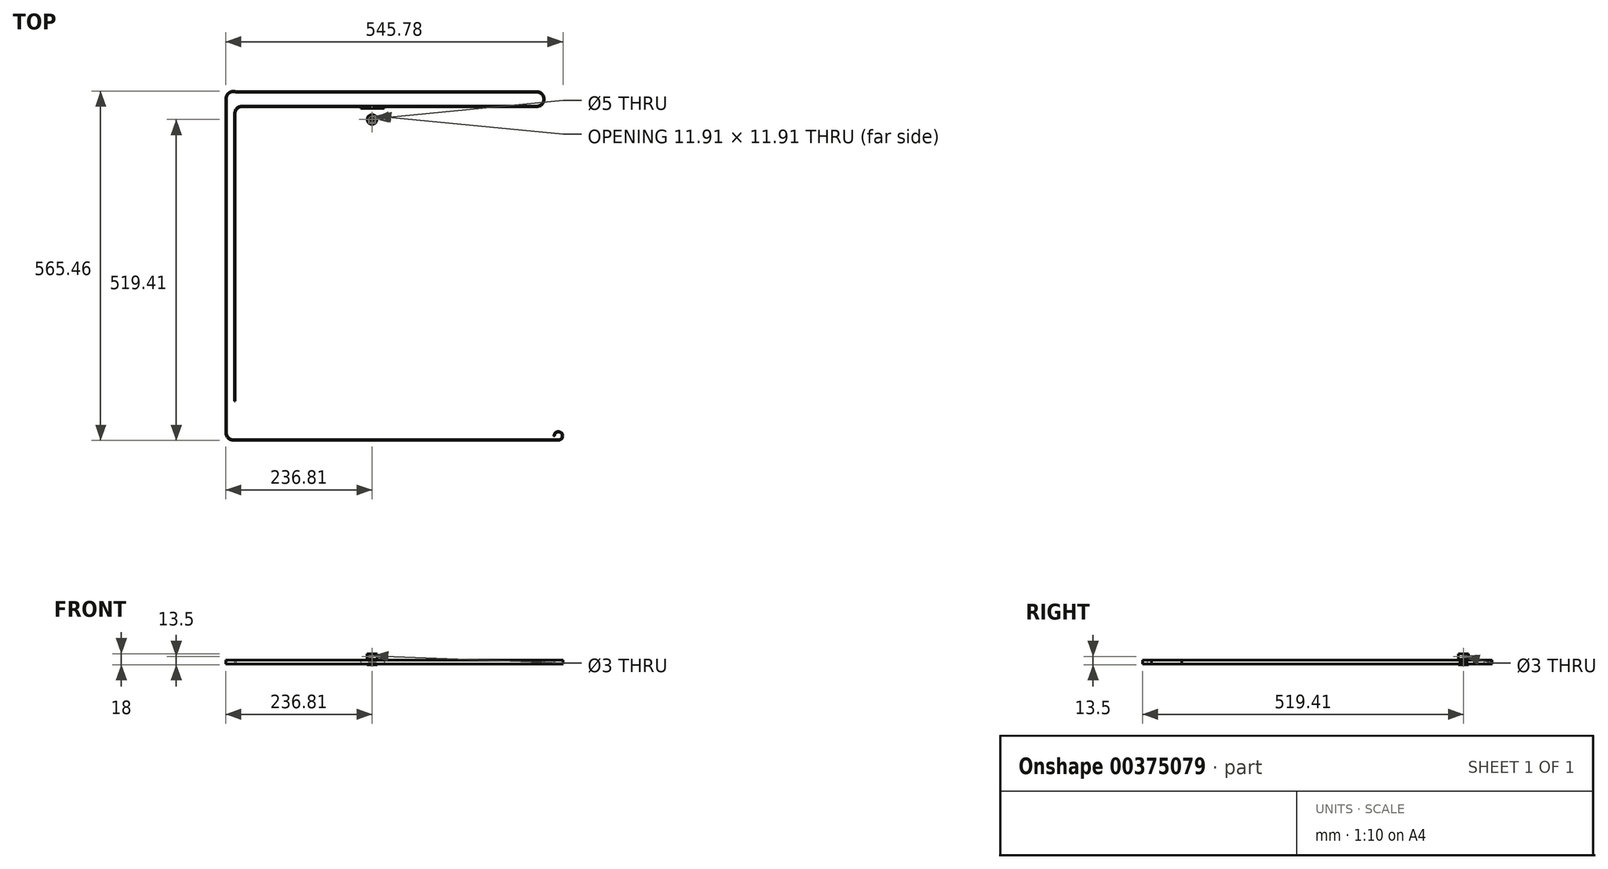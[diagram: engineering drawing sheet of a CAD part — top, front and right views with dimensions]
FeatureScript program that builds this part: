
annotation { "Feature Type Name" : "Feature", "Feature Type Description" : "" }
export const myFeature = defineFeature(function(context is Context, id is Id, definition is map)
    precondition{}
    {
        {
            var Q0;
            Q0=qCreatedBy(makeId("Top.planeOp"),FACE);
            var sketch = newSketch(context, id + "F0", { "sketchPlane" : qUnion([Q0])});
            skLineSegment(sketch, "E0", {"start": v(-19.17, 17.78) * mm, "end": v(-18.17, 17.78) * mm});
            skLineSegment(sketch, "E1", {"start": v(-18.17, 17.78) * mm, "end": v(-18.17, 18.4) * mm});
            skArc(sketch, "E2", {"start": v(-18.67, 18.85) * mm, "mid": v(-18.88, 19.07) * mm, "end": v(-19.17, 19.16) * mm});
            skArc(sketch, "E3", {"start": v(-18.58, 18.54) * mm, "mid": v(-18.61, 18.7) * mm, "end": v(-18.67, 18.85) * mm});
            skArc(sketch, "E4", {"start": v(-18.58, 18.54) * mm, "mid": v(-18.53, 18.44) * mm, "end": v(-18.43, 18.4) * mm});
            skLineSegment(sketch, "E5", {"start": v(-18.43, 18.4) * mm, "end": v(-18.17, 18.4) * mm});
            skArc(sketch, "E6.0.MirrorCS", {"start": v(-19.67, 18.85) * mm, "mid": v(-19.47, 19.07) * mm, "end": v(-19.17, 19.16) * mm});
            skArc(sketch, "E7.0.MirrorCS", {"start": v(-19.76, 18.54) * mm, "mid": v(-19.73, 18.7) * mm, "end": v(-19.67, 18.85) * mm});
            skArc(sketch, "E8.0.MirrorCS", {"start": v(-19.76, 18.54) * mm, "mid": v(-19.81, 18.44) * mm, "end": v(-19.91, 18.4) * mm});
            skLineSegment(sketch, "E9.0.MirrorCS", {"start": v(-19.91, 18.4) * mm, "end": v(-20.17, 18.4) * mm});
            skLineSegment(sketch, "E10.0.MirrorCS", {"start": v(-20.17, 17.78) * mm, "end": v(-20.17, 18.4) * mm});
            skLineSegment(sketch, "E11.0.MirrorCS", {"start": v(-19.17, 17.78) * mm, "end": v(-20.17, 17.78) * mm});
            skLineSegment(sketch, "E12.direction1", {"start": v(-20.17, 17.78) * mm, "end": v(-18.17, 17.78) * mm, "construction": true});
            skLineSegment(sketch, "E13", {"start": v(-20.17, 18.15) * mm, "end": v(-18.17, 18.15) * mm, "construction": true});
            skPoint(sketch, "E14", {"position": v(0, -5.25) * mm});
            skArc(sketch, "E15", {"start": v(0.51, -5.6) * mm, "mid": v(0, -5.25) * mm, "end": v(-0.51, -5.6) * mm});
            skArc(sketch, "E16", {"start": v(-0.51, -5.6) * mm, "mid": v(-0.56, -5.71) * mm, "end": v(-0.59, -5.83) * mm});
            skArc(sketch, "E17", {"start": v(0.59, -5.83) * mm, "mid": v(0.56, -5.71) * mm, "end": v(0.51, -5.6) * mm});
            skArc(sketch, "E18", {"start": v(0.72, -5.96) * mm, "mid": v(0.94, -5.93) * mm, "end": v(1.16, -5.89) * mm});
            skArc(sketch, "E19", {"start": v(0.59, -5.83) * mm, "mid": v(0.66, -5.94) * mm, "end": v(0.8, -5.95) * mm});
            skArc(sketch, "E20", {"start": v(-0.59, -5.83) * mm, "mid": v(-0.66, -5.94) * mm, "end": v(-0.8, -5.95) * mm});
            skArc(sketch, "E21.1.0", {"start": v(2.22, -5.16) * mm, "mid": v(1.62, -5) * mm, "end": v(1.24, -5.48) * mm});
            skPoint(sketch, "E21.1.1", {"position": v(1.62, -5) * mm});
            skArc(sketch, "E21.1.2", {"start": v(1.24, -5.48) * mm, "mid": v(1.23, -5.6) * mm, "end": v(1.24, -5.73) * mm});
            skArc(sketch, "E21.1.3", {"start": v(2.36, -5.37) * mm, "mid": v(2.47, -5.44) * mm, "end": v(2.6, -5.41) * mm});
            skArc(sketch, "E21.1.4", {"start": v(1.24, -5.73) * mm, "mid": v(1.2, -5.85) * mm, "end": v(1.08, -5.9) * mm});
            skArc(sketch, "E21.1.5", {"start": v(2.36, -5.37) * mm, "mid": v(2.3, -5.26) * mm, "end": v(2.22, -5.16) * mm});
            skArc(sketch, "E22.3.2.0", {"start": v(3.7, -4.22) * mm, "mid": v(3.09, -4.25) * mm, "end": v(2.87, -4.83) * mm});
            skPoint(sketch, "E22.4.2.0", {"position": v(3.09, -4.25) * mm});
            skArc(sketch, "E22.5.2.0", {"start": v(2.87, -4.83) * mm, "mid": v(2.9, -4.95) * mm, "end": v(2.95, -5.07) * mm});
            skArc(sketch, "E22.9.2.0", {"start": v(3.9, -4.37) * mm, "mid": v(4.03, -4.41) * mm, "end": v(4.14, -4.35) * mm});
            skArc(sketch, "E22.13.2.0", {"start": v(2.95, -5.07) * mm, "mid": v(2.95, -5.2) * mm, "end": v(2.85, -5.28) * mm});
            skArc(sketch, "E22.17.2.0", {"start": v(3.9, -4.37) * mm, "mid": v(3.81, -4.3) * mm, "end": v(3.7, -4.22) * mm});
            skArc(sketch, "E22.3.3.0", {"start": v(4.83, -2.87) * mm, "mid": v(4.25, -3.09) * mm, "end": v(4.22, -3.7) * mm});
            skPoint(sketch, "E22.4.3.0", {"position": v(4.25, -3.09) * mm});
            skArc(sketch, "E22.5.3.0", {"start": v(4.22, -3.7) * mm, "mid": v(4.3, -3.81) * mm, "end": v(4.37, -3.9) * mm});
            skArc(sketch, "E22.9.3.0", {"start": v(5.07, -2.95) * mm, "mid": v(5.2, -2.95) * mm, "end": v(5.28, -2.85) * mm});
            skArc(sketch, "E22.13.3.0", {"start": v(4.37, -3.9) * mm, "mid": v(4.41, -4.03) * mm, "end": v(4.35, -4.14) * mm});
            skArc(sketch, "E22.17.3.0", {"start": v(5.07, -2.95) * mm, "mid": v(4.95, -2.9) * mm, "end": v(4.83, -2.87) * mm});
            skArc(sketch, "E22.3.4.0", {"start": v(5.48, -1.24) * mm, "mid": v(5, -1.62) * mm, "end": v(5.16, -2.22) * mm});
            skPoint(sketch, "E22.4.4.0", {"position": v(5, -1.62) * mm});
            skArc(sketch, "E22.5.4.0", {"start": v(5.16, -2.22) * mm, "mid": v(5.26, -2.3) * mm, "end": v(5.37, -2.36) * mm});
            skArc(sketch, "E22.9.4.0", {"start": v(5.73, -1.24) * mm, "mid": v(5.85, -1.2) * mm, "end": v(5.9, -1.08) * mm});
            skArc(sketch, "E22.13.4.0", {"start": v(5.37, -2.36) * mm, "mid": v(5.44, -2.47) * mm, "end": v(5.41, -2.6) * mm});
            skArc(sketch, "E22.17.4.0", {"start": v(5.73, -1.24) * mm, "mid": v(5.6, -1.23) * mm, "end": v(5.48, -1.24) * mm});
            skArc(sketch, "E22.3.5.0", {"start": v(5.6, 0.51) * mm, "mid": v(5.25, 0) * mm, "end": v(5.6, -0.51) * mm});
            skPoint(sketch, "E22.4.5.0", {"position": v(5.25, 0) * mm});
            skArc(sketch, "E22.5.5.0", {"start": v(5.6, -0.51) * mm, "mid": v(5.71, -0.56) * mm, "end": v(5.83, -0.59) * mm});
            skArc(sketch, "E22.9.5.0", {"start": v(5.83, 0.59) * mm, "mid": v(5.94, 0.66) * mm, "end": v(5.95, 0.8) * mm});
            skArc(sketch, "E22.13.5.0", {"start": v(5.83, -0.59) * mm, "mid": v(5.94, -0.66) * mm, "end": v(5.95, -0.8) * mm});
            skArc(sketch, "E22.17.5.0", {"start": v(5.83, 0.59) * mm, "mid": v(5.71, 0.56) * mm, "end": v(5.6, 0.51) * mm});
            skArc(sketch, "E22.3.6.0", {"start": v(5.16, 2.22) * mm, "mid": v(5, 1.62) * mm, "end": v(5.48, 1.24) * mm});
            skPoint(sketch, "E22.4.6.0", {"position": v(5, 1.62) * mm});
            skArc(sketch, "E22.5.6.0", {"start": v(5.48, 1.24) * mm, "mid": v(5.6, 1.23) * mm, "end": v(5.73, 1.24) * mm});
            skArc(sketch, "E22.9.6.0", {"start": v(5.37, 2.36) * mm, "mid": v(5.44, 2.47) * mm, "end": v(5.41, 2.6) * mm});
            skArc(sketch, "E22.13.6.0", {"start": v(5.73, 1.24) * mm, "mid": v(5.85, 1.2) * mm, "end": v(5.9, 1.08) * mm});
            skArc(sketch, "E22.17.6.0", {"start": v(5.37, 2.36) * mm, "mid": v(5.26, 2.3) * mm, "end": v(5.16, 2.22) * mm});
            skArc(sketch, "E22.3.7.0", {"start": v(4.22, 3.7) * mm, "mid": v(4.25, 3.09) * mm, "end": v(4.83, 2.87) * mm});
            skPoint(sketch, "E22.4.7.0", {"position": v(4.25, 3.09) * mm});
            skArc(sketch, "E22.5.7.0", {"start": v(4.83, 2.87) * mm, "mid": v(4.95, 2.9) * mm, "end": v(5.07, 2.95) * mm});
            skArc(sketch, "E22.9.7.0", {"start": v(4.37, 3.9) * mm, "mid": v(4.41, 4.03) * mm, "end": v(4.35, 4.14) * mm});
            skArc(sketch, "E22.13.7.0", {"start": v(5.07, 2.95) * mm, "mid": v(5.2, 2.95) * mm, "end": v(5.28, 2.85) * mm});
            skArc(sketch, "E22.17.7.0", {"start": v(4.37, 3.9) * mm, "mid": v(4.3, 3.81) * mm, "end": v(4.22, 3.7) * mm});
            skArc(sketch, "E22.3.8.0", {"start": v(2.87, 4.83) * mm, "mid": v(3.09, 4.25) * mm, "end": v(3.7, 4.22) * mm});
            skPoint(sketch, "E22.4.8.0", {"position": v(3.09, 4.25) * mm});
            skArc(sketch, "E22.5.8.0", {"start": v(3.7, 4.22) * mm, "mid": v(3.81, 4.3) * mm, "end": v(3.9, 4.37) * mm});
            skArc(sketch, "E22.9.8.0", {"start": v(2.95, 5.07) * mm, "mid": v(2.95, 5.2) * mm, "end": v(2.85, 5.28) * mm});
            skArc(sketch, "E22.13.8.0", {"start": v(3.9, 4.37) * mm, "mid": v(4.03, 4.41) * mm, "end": v(4.14, 4.35) * mm});
            skArc(sketch, "E22.17.8.0", {"start": v(2.95, 5.07) * mm, "mid": v(2.9, 4.95) * mm, "end": v(2.87, 4.83) * mm});
            skArc(sketch, "E22.3.9.0", {"start": v(1.24, 5.48) * mm, "mid": v(1.62, 5) * mm, "end": v(2.22, 5.16) * mm});
            skPoint(sketch, "E22.4.9.0", {"position": v(1.62, 5) * mm});
            skArc(sketch, "E22.5.9.0", {"start": v(2.22, 5.16) * mm, "mid": v(2.3, 5.26) * mm, "end": v(2.36, 5.37) * mm});
            skArc(sketch, "E22.9.9.0", {"start": v(1.24, 5.73) * mm, "mid": v(1.2, 5.85) * mm, "end": v(1.08, 5.9) * mm});
            skArc(sketch, "E22.13.9.0", {"start": v(2.36, 5.37) * mm, "mid": v(2.47, 5.44) * mm, "end": v(2.6, 5.41) * mm});
            skArc(sketch, "E22.17.9.0", {"start": v(1.24, 5.73) * mm, "mid": v(1.23, 5.6) * mm, "end": v(1.24, 5.48) * mm});
            skArc(sketch, "E22.3.10.0", {"start": v(-0.51, 5.6) * mm, "mid": v(0, 5.25) * mm, "end": v(0.51, 5.6) * mm});
            skPoint(sketch, "E22.4.10.0", {"position": v(0, 5.25) * mm});
            skArc(sketch, "E22.5.10.0", {"start": v(0.51, 5.6) * mm, "mid": v(0.56, 5.71) * mm, "end": v(0.59, 5.83) * mm});
            skArc(sketch, "E22.9.10.0", {"start": v(-0.59, 5.83) * mm, "mid": v(-0.66, 5.94) * mm, "end": v(-0.8, 5.95) * mm});
            skArc(sketch, "E22.13.10.0", {"start": v(0.59, 5.83) * mm, "mid": v(0.66, 5.94) * mm, "end": v(0.8, 5.95) * mm});
            skArc(sketch, "E22.17.10.0", {"start": v(-0.59, 5.83) * mm, "mid": v(-0.56, 5.71) * mm, "end": v(-0.51, 5.6) * mm});
            skArc(sketch, "E22.3.11.0", {"start": v(-2.22, 5.16) * mm, "mid": v(-1.62, 5) * mm, "end": v(-1.24, 5.48) * mm});
            skPoint(sketch, "E22.4.11.0", {"position": v(-1.62, 5) * mm});
            skArc(sketch, "E22.5.11.0", {"start": v(-1.24, 5.48) * mm, "mid": v(-1.23, 5.6) * mm, "end": v(-1.24, 5.73) * mm});
            skArc(sketch, "E22.9.11.0", {"start": v(-2.36, 5.37) * mm, "mid": v(-2.47, 5.44) * mm, "end": v(-2.6, 5.41) * mm});
            skArc(sketch, "E22.13.11.0", {"start": v(-1.24, 5.73) * mm, "mid": v(-1.2, 5.85) * mm, "end": v(-1.08, 5.9) * mm});
            skArc(sketch, "E22.17.11.0", {"start": v(-2.36, 5.37) * mm, "mid": v(-2.3, 5.26) * mm, "end": v(-2.22, 5.16) * mm});
            skArc(sketch, "E22.3.12.0", {"start": v(-3.7, 4.22) * mm, "mid": v(-3.09, 4.25) * mm, "end": v(-2.87, 4.83) * mm});
            skPoint(sketch, "E22.4.12.0", {"position": v(-3.09, 4.25) * mm});
            skArc(sketch, "E22.5.12.0", {"start": v(-2.87, 4.83) * mm, "mid": v(-2.9, 4.95) * mm, "end": v(-2.95, 5.07) * mm});
            skArc(sketch, "E22.9.12.0", {"start": v(-3.9, 4.37) * mm, "mid": v(-4.03, 4.41) * mm, "end": v(-4.14, 4.35) * mm});
            skArc(sketch, "E22.13.12.0", {"start": v(-2.95, 5.07) * mm, "mid": v(-2.95, 5.2) * mm, "end": v(-2.85, 5.28) * mm});
            skArc(sketch, "E22.17.12.0", {"start": v(-3.9, 4.37) * mm, "mid": v(-3.81, 4.3) * mm, "end": v(-3.7, 4.22) * mm});
            skArc(sketch, "E22.3.13.0", {"start": v(-4.83, 2.87) * mm, "mid": v(-4.25, 3.09) * mm, "end": v(-4.22, 3.7) * mm});
            skPoint(sketch, "E22.4.13.0", {"position": v(-4.25, 3.09) * mm});
            skArc(sketch, "E22.5.13.0", {"start": v(-4.22, 3.7) * mm, "mid": v(-4.3, 3.81) * mm, "end": v(-4.37, 3.9) * mm});
            skArc(sketch, "E22.9.13.0", {"start": v(-5.07, 2.95) * mm, "mid": v(-5.2, 2.95) * mm, "end": v(-5.28, 2.85) * mm});
            skArc(sketch, "E22.13.13.0", {"start": v(-4.37, 3.9) * mm, "mid": v(-4.41, 4.03) * mm, "end": v(-4.35, 4.14) * mm});
            skArc(sketch, "E22.17.13.0", {"start": v(-5.07, 2.95) * mm, "mid": v(-4.95, 2.9) * mm, "end": v(-4.83, 2.87) * mm});
            skArc(sketch, "E22.3.14.0", {"start": v(-5.48, 1.24) * mm, "mid": v(-5, 1.62) * mm, "end": v(-5.16, 2.22) * mm});
            skPoint(sketch, "E22.4.14.0", {"position": v(-5, 1.62) * mm});
            skArc(sketch, "E22.5.14.0", {"start": v(-5.16, 2.22) * mm, "mid": v(-5.26, 2.3) * mm, "end": v(-5.37, 2.36) * mm});
            skArc(sketch, "E22.9.14.0", {"start": v(-5.73, 1.24) * mm, "mid": v(-5.85, 1.2) * mm, "end": v(-5.9, 1.08) * mm});
            skArc(sketch, "E22.13.14.0", {"start": v(-5.37, 2.36) * mm, "mid": v(-5.44, 2.47) * mm, "end": v(-5.41, 2.6) * mm});
            skArc(sketch, "E22.17.14.0", {"start": v(-5.73, 1.24) * mm, "mid": v(-5.6, 1.23) * mm, "end": v(-5.48, 1.24) * mm});
            skArc(sketch, "E22.3.15.0", {"start": v(-5.6, -0.51) * mm, "mid": v(-5.25, 0) * mm, "end": v(-5.6, 0.51) * mm});
            skPoint(sketch, "E22.4.15.0", {"position": v(-5.25, 0) * mm});
            skArc(sketch, "E22.5.15.0", {"start": v(-5.6, 0.51) * mm, "mid": v(-5.71, 0.56) * mm, "end": v(-5.83, 0.59) * mm});
            skArc(sketch, "E22.9.15.0", {"start": v(-5.83, -0.59) * mm, "mid": v(-5.94, -0.66) * mm, "end": v(-5.95, -0.8) * mm});
            skArc(sketch, "E22.13.15.0", {"start": v(-5.83, 0.59) * mm, "mid": v(-5.94, 0.66) * mm, "end": v(-5.95, 0.8) * mm});
            skArc(sketch, "E22.17.15.0", {"start": v(-5.83, -0.59) * mm, "mid": v(-5.71, -0.56) * mm, "end": v(-5.6, -0.51) * mm});
            skArc(sketch, "E22.3.16.0", {"start": v(-5.16, -2.22) * mm, "mid": v(-5, -1.62) * mm, "end": v(-5.48, -1.24) * mm});
            skPoint(sketch, "E22.4.16.0", {"position": v(-5, -1.62) * mm});
            skArc(sketch, "E22.5.16.0", {"start": v(-5.48, -1.24) * mm, "mid": v(-5.6, -1.23) * mm, "end": v(-5.73, -1.24) * mm});
            skArc(sketch, "E22.9.16.0", {"start": v(-5.37, -2.36) * mm, "mid": v(-5.44, -2.47) * mm, "end": v(-5.41, -2.6) * mm});
            skArc(sketch, "E22.13.16.0", {"start": v(-5.73, -1.24) * mm, "mid": v(-5.85, -1.2) * mm, "end": v(-5.9, -1.08) * mm});
            skArc(sketch, "E22.17.16.0", {"start": v(-5.37, -2.36) * mm, "mid": v(-5.26, -2.3) * mm, "end": v(-5.16, -2.22) * mm});
            skArc(sketch, "E22.3.17.0", {"start": v(-4.22, -3.7) * mm, "mid": v(-4.25, -3.09) * mm, "end": v(-4.83, -2.87) * mm});
            skPoint(sketch, "E22.4.17.0", {"position": v(-4.25, -3.09) * mm});
            skArc(sketch, "E22.5.17.0", {"start": v(-4.83, -2.87) * mm, "mid": v(-4.95, -2.9) * mm, "end": v(-5.07, -2.95) * mm});
            skArc(sketch, "E22.9.17.0", {"start": v(-4.37, -3.9) * mm, "mid": v(-4.41, -4.03) * mm, "end": v(-4.35, -4.14) * mm});
            skArc(sketch, "E22.13.17.0", {"start": v(-5.07, -2.95) * mm, "mid": v(-5.2, -2.95) * mm, "end": v(-5.28, -2.85) * mm});
            skArc(sketch, "E22.17.17.0", {"start": v(-4.37, -3.9) * mm, "mid": v(-4.3, -3.81) * mm, "end": v(-4.22, -3.7) * mm});
            skArc(sketch, "E22.3.18.0", {"start": v(-2.87, -4.83) * mm, "mid": v(-3.09, -4.25) * mm, "end": v(-3.7, -4.22) * mm});
            skPoint(sketch, "E22.4.18.0", {"position": v(-3.09, -4.25) * mm});
            skArc(sketch, "E22.5.18.0", {"start": v(-3.7, -4.22) * mm, "mid": v(-3.81, -4.3) * mm, "end": v(-3.9, -4.37) * mm});
            skArc(sketch, "E22.9.18.0", {"start": v(-2.95, -5.07) * mm, "mid": v(-2.95, -5.2) * mm, "end": v(-2.85, -5.28) * mm});
            skArc(sketch, "E22.13.18.0", {"start": v(-3.9, -4.37) * mm, "mid": v(-4.03, -4.41) * mm, "end": v(-4.14, -4.35) * mm});
            skArc(sketch, "E22.17.18.0", {"start": v(-2.95, -5.07) * mm, "mid": v(-2.9, -4.95) * mm, "end": v(-2.87, -4.83) * mm});
            skArc(sketch, "E22.3.19.0", {"start": v(-1.24, -5.48) * mm, "mid": v(-1.62, -5) * mm, "end": v(-2.22, -5.16) * mm});
            skPoint(sketch, "E22.4.19.0", {"position": v(-1.62, -5) * mm});
            skArc(sketch, "E22.5.19.0", {"start": v(-2.22, -5.16) * mm, "mid": v(-2.3, -5.26) * mm, "end": v(-2.36, -5.37) * mm});
            skArc(sketch, "E22.9.19.0", {"start": v(-1.24, -5.73) * mm, "mid": v(-1.2, -5.85) * mm, "end": v(-1.08, -5.9) * mm});
            skArc(sketch, "E22.13.19.0", {"start": v(-2.36, -5.37) * mm, "mid": v(-2.47, -5.44) * mm, "end": v(-2.6, -5.41) * mm});
            skArc(sketch, "E22.17.19.0", {"start": v(-1.24, -5.73) * mm, "mid": v(-1.23, -5.6) * mm, "end": v(-1.24, -5.48) * mm});
            skArc(sketch, "E23.trimOffspring", {"start": v(2.52, -5.44) * mm, "mid": v(2.72, -5.35) * mm, "end": v(2.92, -5.24) * mm});
            skArc(sketch, "E24.trimOffspring", {"start": v(4.08, -4.4) * mm, "mid": v(4.24, -4.24) * mm, "end": v(4.4, -4.08) * mm});
            skArc(sketch, "E25.trimOffspring", {"start": v(5.24, -2.92) * mm, "mid": v(5.33, -2.76) * mm, "end": v(5.41, -2.6) * mm});
            skArc(sketch, "E26.trimOffspring", {"start": v(5.89, -1.16) * mm, "mid": v(5.93, -0.94) * mm, "end": v(5.96, -0.72) * mm});
            skArc(sketch, "E27.trimOffspring", {"start": v(5.44, 2.52) * mm, "mid": v(5.35, 2.72) * mm, "end": v(5.24, 2.92) * mm});
            skArc(sketch, "E28.trimOffspring", {"start": v(4.4, 4.08) * mm, "mid": v(4.24, 4.24) * mm, "end": v(4.08, 4.4) * mm});
            skArc(sketch, "E29.trimOffspring", {"start": v(5.96, 0.72) * mm, "mid": v(5.93, 0.94) * mm, "end": v(5.89, 1.16) * mm});
            skArc(sketch, "E30.trimOffspring", {"start": v(2.92, 5.24) * mm, "mid": v(2.72, 5.35) * mm, "end": v(2.52, 5.44) * mm});
            skArc(sketch, "E31.trimOffspring", {"start": v(1.16, 5.89) * mm, "mid": v(0.94, 5.93) * mm, "end": v(0.72, 5.96) * mm});
            skArc(sketch, "E32.trimOffspring", {"start": v(-0.72, 5.96) * mm, "mid": v(-0.94, 5.93) * mm, "end": v(-1.16, 5.89) * mm});
            skArc(sketch, "E33.trimOffspring", {"start": v(-2.52, 5.44) * mm, "mid": v(-2.72, 5.35) * mm, "end": v(-2.92, 5.24) * mm});
            skArc(sketch, "E34.trimOffspring", {"start": v(-4.08, 4.4) * mm, "mid": v(-4.24, 4.24) * mm, "end": v(-4.4, 4.08) * mm});
            skArc(sketch, "E35.trimOffspring", {"start": v(-5.24, 2.92) * mm, "mid": v(-5.35, 2.72) * mm, "end": v(-5.44, 2.52) * mm});
            skArc(sketch, "E36.trimOffspring", {"start": v(-5.89, 1.16) * mm, "mid": v(-5.93, 0.94) * mm, "end": v(-5.96, 0.72) * mm});
            skArc(sketch, "E37.trimOffspring", {"start": v(-5.96, -0.72) * mm, "mid": v(-5.93, -0.94) * mm, "end": v(-5.89, -1.16) * mm});
            skArc(sketch, "E38.trimOffspring", {"start": v(-5.44, -2.52) * mm, "mid": v(-5.35, -2.72) * mm, "end": v(-5.24, -2.92) * mm});
            skArc(sketch, "E39.trimOffspring", {"start": v(-4.4, -4.08) * mm, "mid": v(-4.24, -4.24) * mm, "end": v(-4.08, -4.4) * mm});
            skArc(sketch, "E40.trimOffspring", {"start": v(-2.92, -5.24) * mm, "mid": v(-2.72, -5.35) * mm, "end": v(-2.52, -5.44) * mm});
            skArc(sketch, "E41.trimOffspring", {"start": v(-1.16, -5.89) * mm, "mid": v(-0.94, -5.93) * mm, "end": v(-0.72, -5.96) * mm});
            skArc(sketch, "E42.1.0.0", {"start": v(-16.67, 18.85) * mm, "mid": v(-16.88, 19.07) * mm, "end": v(-17.17, 19.16) * mm});
            skArc(sketch, "E42.1.0.1", {"start": v(-16.58, 18.54) * mm, "mid": v(-16.61, 18.7) * mm, "end": v(-16.67, 18.85) * mm});
            skArc(sketch, "E42.1.0.2", {"start": v(-16.58, 18.54) * mm, "mid": v(-16.53, 18.44) * mm, "end": v(-16.43, 18.4) * mm});
            skLineSegment(sketch, "E42.1.0.3", {"start": v(-16.43, 18.4) * mm, "end": v(-16.17, 18.4) * mm});
            skArc(sketch, "E42.1.0.4", {"start": v(-17.67, 18.85) * mm, "mid": v(-17.47, 19.07) * mm, "end": v(-17.17, 19.16) * mm});
            skArc(sketch, "E42.1.0.5", {"start": v(-17.76, 18.54) * mm, "mid": v(-17.73, 18.7) * mm, "end": v(-17.67, 18.85) * mm});
            skArc(sketch, "E42.1.0.6", {"start": v(-17.76, 18.54) * mm, "mid": v(-17.81, 18.44) * mm, "end": v(-17.91, 18.4) * mm});
            skLineSegment(sketch, "E42.1.0.7", {"start": v(-17.91, 18.4) * mm, "end": v(-18.17, 18.4) * mm});
            skArc(sketch, "E42.2.0.0", {"start": v(-14.67, 18.85) * mm, "mid": v(-14.88, 19.07) * mm, "end": v(-15.17, 19.16) * mm});
            skArc(sketch, "E42.2.0.1", {"start": v(-14.58, 18.54) * mm, "mid": v(-14.61, 18.7) * mm, "end": v(-14.67, 18.85) * mm});
            skArc(sketch, "E42.2.0.2", {"start": v(-14.58, 18.54) * mm, "mid": v(-14.53, 18.44) * mm, "end": v(-14.43, 18.4) * mm});
            skLineSegment(sketch, "E42.2.0.3", {"start": v(-14.43, 18.4) * mm, "end": v(-14.17, 18.4) * mm});
            skArc(sketch, "E42.2.0.4", {"start": v(-15.67, 18.85) * mm, "mid": v(-15.47, 19.07) * mm, "end": v(-15.17, 19.16) * mm});
            skArc(sketch, "E42.2.0.5", {"start": v(-15.76, 18.54) * mm, "mid": v(-15.73, 18.7) * mm, "end": v(-15.67, 18.85) * mm});
            skArc(sketch, "E42.2.0.6", {"start": v(-15.76, 18.54) * mm, "mid": v(-15.81, 18.44) * mm, "end": v(-15.91, 18.4) * mm});
            skLineSegment(sketch, "E42.2.0.7", {"start": v(-15.91, 18.4) * mm, "end": v(-16.17, 18.4) * mm});
            skArc(sketch, "E42.3.0.0", {"start": v(-12.67, 18.85) * mm, "mid": v(-12.88, 19.07) * mm, "end": v(-13.17, 19.16) * mm});
            skArc(sketch, "E42.3.0.1", {"start": v(-12.58, 18.54) * mm, "mid": v(-12.61, 18.7) * mm, "end": v(-12.67, 18.85) * mm});
            skArc(sketch, "E42.3.0.2", {"start": v(-12.58, 18.54) * mm, "mid": v(-12.53, 18.44) * mm, "end": v(-12.43, 18.4) * mm});
            skLineSegment(sketch, "E42.3.0.3", {"start": v(-12.43, 18.4) * mm, "end": v(-12.17, 18.4) * mm});
            skArc(sketch, "E42.3.0.4", {"start": v(-13.67, 18.85) * mm, "mid": v(-13.47, 19.07) * mm, "end": v(-13.17, 19.16) * mm});
            skArc(sketch, "E42.3.0.5", {"start": v(-13.76, 18.54) * mm, "mid": v(-13.73, 18.7) * mm, "end": v(-13.67, 18.85) * mm});
            skArc(sketch, "E42.3.0.6", {"start": v(-13.76, 18.54) * mm, "mid": v(-13.81, 18.44) * mm, "end": v(-13.91, 18.4) * mm});
            skLineSegment(sketch, "E42.3.0.7", {"start": v(-13.91, 18.4) * mm, "end": v(-14.17, 18.4) * mm});
            skArc(sketch, "E42.4.0.0", {"start": v(-10.67, 18.85) * mm, "mid": v(-10.88, 19.07) * mm, "end": v(-11.17, 19.16) * mm});
            skArc(sketch, "E42.4.0.1", {"start": v(-10.58, 18.54) * mm, "mid": v(-10.61, 18.7) * mm, "end": v(-10.67, 18.85) * mm});
            skArc(sketch, "E42.4.0.2", {"start": v(-10.58, 18.54) * mm, "mid": v(-10.53, 18.44) * mm, "end": v(-10.43, 18.4) * mm});
            skLineSegment(sketch, "E42.4.0.3", {"start": v(-10.43, 18.4) * mm, "end": v(-10.17, 18.4) * mm});
            skArc(sketch, "E42.4.0.4", {"start": v(-11.67, 18.85) * mm, "mid": v(-11.47, 19.07) * mm, "end": v(-11.17, 19.16) * mm});
            skArc(sketch, "E42.4.0.5", {"start": v(-11.76, 18.54) * mm, "mid": v(-11.73, 18.7) * mm, "end": v(-11.67, 18.85) * mm});
            skArc(sketch, "E42.4.0.6", {"start": v(-11.76, 18.54) * mm, "mid": v(-11.81, 18.44) * mm, "end": v(-11.91, 18.4) * mm});
            skLineSegment(sketch, "E42.4.0.7", {"start": v(-11.91, 18.4) * mm, "end": v(-12.17, 18.4) * mm});
            skArc(sketch, "E42.5.0.0", {"start": v(-8.67, 18.85) * mm, "mid": v(-8.88, 19.07) * mm, "end": v(-9.17, 19.16) * mm});
            skArc(sketch, "E42.5.0.1", {"start": v(-8.58, 18.54) * mm, "mid": v(-8.61, 18.7) * mm, "end": v(-8.67, 18.85) * mm});
            skArc(sketch, "E42.5.0.2", {"start": v(-8.58, 18.54) * mm, "mid": v(-8.53, 18.44) * mm, "end": v(-8.43, 18.4) * mm});
            skLineSegment(sketch, "E42.5.0.3", {"start": v(-8.43, 18.4) * mm, "end": v(-8.17, 18.4) * mm});
            skArc(sketch, "E42.5.0.4", {"start": v(-9.67, 18.85) * mm, "mid": v(-9.47, 19.07) * mm, "end": v(-9.17, 19.16) * mm});
            skArc(sketch, "E42.5.0.5", {"start": v(-9.76, 18.54) * mm, "mid": v(-9.73, 18.7) * mm, "end": v(-9.67, 18.85) * mm});
            skArc(sketch, "E42.5.0.6", {"start": v(-9.76, 18.54) * mm, "mid": v(-9.81, 18.44) * mm, "end": v(-9.91, 18.4) * mm});
            skLineSegment(sketch, "E42.5.0.7", {"start": v(-9.91, 18.4) * mm, "end": v(-10.17, 18.4) * mm});
            skArc(sketch, "E42.6.0.0", {"start": v(-6.67, 18.85) * mm, "mid": v(-6.88, 19.07) * mm, "end": v(-7.17, 19.16) * mm});
            skArc(sketch, "E42.6.0.1", {"start": v(-6.58, 18.54) * mm, "mid": v(-6.61, 18.7) * mm, "end": v(-6.67, 18.85) * mm});
            skArc(sketch, "E42.6.0.2", {"start": v(-6.58, 18.54) * mm, "mid": v(-6.53, 18.44) * mm, "end": v(-6.43, 18.4) * mm});
            skLineSegment(sketch, "E42.6.0.3", {"start": v(-6.43, 18.4) * mm, "end": v(-6.17, 18.4) * mm});
            skArc(sketch, "E42.6.0.4", {"start": v(-7.67, 18.85) * mm, "mid": v(-7.47, 19.07) * mm, "end": v(-7.17, 19.16) * mm});
            skArc(sketch, "E42.6.0.5", {"start": v(-7.76, 18.54) * mm, "mid": v(-7.73, 18.7) * mm, "end": v(-7.67, 18.85) * mm});
            skArc(sketch, "E42.6.0.6", {"start": v(-7.76, 18.54) * mm, "mid": v(-7.81, 18.44) * mm, "end": v(-7.91, 18.4) * mm});
            skLineSegment(sketch, "E42.6.0.7", {"start": v(-7.91, 18.4) * mm, "end": v(-8.17, 18.4) * mm});
            skArc(sketch, "E42.7.0.0", {"start": v(-4.67, 18.85) * mm, "mid": v(-4.88, 19.07) * mm, "end": v(-5.17, 19.16) * mm});
            skArc(sketch, "E42.7.0.1", {"start": v(-4.58, 18.54) * mm, "mid": v(-4.61, 18.7) * mm, "end": v(-4.67, 18.85) * mm});
            skArc(sketch, "E42.7.0.2", {"start": v(-4.58, 18.54) * mm, "mid": v(-4.53, 18.44) * mm, "end": v(-4.43, 18.4) * mm});
            skLineSegment(sketch, "E42.7.0.3", {"start": v(-4.43, 18.4) * mm, "end": v(-4.17, 18.4) * mm});
            skArc(sketch, "E42.7.0.4", {"start": v(-5.67, 18.85) * mm, "mid": v(-5.47, 19.07) * mm, "end": v(-5.17, 19.16) * mm});
            skArc(sketch, "E42.7.0.5", {"start": v(-5.76, 18.54) * mm, "mid": v(-5.73, 18.7) * mm, "end": v(-5.67, 18.85) * mm});
            skArc(sketch, "E42.7.0.6", {"start": v(-5.76, 18.54) * mm, "mid": v(-5.81, 18.44) * mm, "end": v(-5.91, 18.4) * mm});
            skLineSegment(sketch, "E42.7.0.7", {"start": v(-5.91, 18.4) * mm, "end": v(-6.17, 18.4) * mm});
            skArc(sketch, "E42.8.0.0", {"start": v(-2.67, 18.85) * mm, "mid": v(-2.88, 19.07) * mm, "end": v(-3.17, 19.16) * mm});
            skArc(sketch, "E42.8.0.1", {"start": v(-2.58, 18.54) * mm, "mid": v(-2.61, 18.7) * mm, "end": v(-2.67, 18.85) * mm});
            skArc(sketch, "E42.8.0.2", {"start": v(-2.58, 18.54) * mm, "mid": v(-2.53, 18.44) * mm, "end": v(-2.43, 18.4) * mm});
            skLineSegment(sketch, "E42.8.0.3", {"start": v(-2.43, 18.4) * mm, "end": v(-2.17, 18.4) * mm});
            skArc(sketch, "E42.8.0.4", {"start": v(-3.67, 18.85) * mm, "mid": v(-3.47, 19.07) * mm, "end": v(-3.17, 19.16) * mm});
            skArc(sketch, "E42.8.0.5", {"start": v(-3.76, 18.54) * mm, "mid": v(-3.73, 18.7) * mm, "end": v(-3.67, 18.85) * mm});
            skArc(sketch, "E42.8.0.6", {"start": v(-3.76, 18.54) * mm, "mid": v(-3.81, 18.44) * mm, "end": v(-3.91, 18.4) * mm});
            skLineSegment(sketch, "E42.8.0.7", {"start": v(-3.91, 18.4) * mm, "end": v(-4.17, 18.4) * mm});
            skArc(sketch, "E42.9.0.0", {"start": v(-0.67, 18.85) * mm, "mid": v(-0.88, 19.07) * mm, "end": v(-1.17, 19.16) * mm});
            skArc(sketch, "E42.9.0.1", {"start": v(-0.58, 18.54) * mm, "mid": v(-0.61, 18.7) * mm, "end": v(-0.67, 18.85) * mm});
            skArc(sketch, "E42.9.0.2", {"start": v(-0.58, 18.54) * mm, "mid": v(-0.53, 18.44) * mm, "end": v(-0.43, 18.4) * mm});
            skLineSegment(sketch, "E42.9.0.3", {"start": v(-0.43, 18.4) * mm, "end": v(-0.17, 18.4) * mm});
            skArc(sketch, "E42.9.0.4", {"start": v(-1.67, 18.85) * mm, "mid": v(-1.47, 19.07) * mm, "end": v(-1.17, 19.16) * mm});
            skArc(sketch, "E42.9.0.5", {"start": v(-1.76, 18.54) * mm, "mid": v(-1.73, 18.7) * mm, "end": v(-1.67, 18.85) * mm});
            skArc(sketch, "E42.9.0.6", {"start": v(-1.76, 18.54) * mm, "mid": v(-1.81, 18.44) * mm, "end": v(-1.91, 18.4) * mm});
            skLineSegment(sketch, "E42.9.0.7", {"start": v(-1.91, 18.4) * mm, "end": v(-2.17, 18.4) * mm});
            skArc(sketch, "E42.10.0.0", {"start": v(1.33, 18.85) * mm, "mid": v(1.12, 19.07) * mm, "end": v(0.83, 19.16) * mm});
            skArc(sketch, "E42.10.0.1", {"start": v(1.42, 18.54) * mm, "mid": v(1.39, 18.7) * mm, "end": v(1.33, 18.85) * mm});
            skArc(sketch, "E42.10.0.2", {"start": v(1.42, 18.54) * mm, "mid": v(1.47, 18.44) * mm, "end": v(1.57, 18.4) * mm});
            skLineSegment(sketch, "E42.10.0.3", {"start": v(1.57, 18.4) * mm, "end": v(1.83, 18.4) * mm});
            skArc(sketch, "E42.10.0.4", {"start": v(0.33, 18.85) * mm, "mid": v(0.53, 19.07) * mm, "end": v(0.83, 19.16) * mm});
            skArc(sketch, "E42.10.0.5", {"start": v(0.24, 18.54) * mm, "mid": v(0.27, 18.7) * mm, "end": v(0.33, 18.85) * mm});
            skArc(sketch, "E42.10.0.6", {"start": v(0.24, 18.54) * mm, "mid": v(0.19, 18.44) * mm, "end": v(0.09, 18.4) * mm});
            skLineSegment(sketch, "E42.10.0.7", {"start": v(0.09, 18.4) * mm, "end": v(-0.17, 18.4) * mm});
            skArc(sketch, "E42.11.0.0", {"start": v(3.33, 18.85) * mm, "mid": v(3.12, 19.07) * mm, "end": v(2.83, 19.16) * mm});
            skArc(sketch, "E42.11.0.1", {"start": v(3.42, 18.54) * mm, "mid": v(3.39, 18.7) * mm, "end": v(3.33, 18.85) * mm});
            skArc(sketch, "E42.11.0.2", {"start": v(3.42, 18.54) * mm, "mid": v(3.47, 18.44) * mm, "end": v(3.57, 18.4) * mm});
            skLineSegment(sketch, "E42.11.0.3", {"start": v(3.57, 18.4) * mm, "end": v(3.83, 18.4) * mm});
            skArc(sketch, "E42.11.0.4", {"start": v(2.33, 18.85) * mm, "mid": v(2.53, 19.07) * mm, "end": v(2.83, 19.16) * mm});
            skArc(sketch, "E42.11.0.5", {"start": v(2.24, 18.54) * mm, "mid": v(2.27, 18.7) * mm, "end": v(2.33, 18.85) * mm});
            skArc(sketch, "E42.11.0.6", {"start": v(2.24, 18.54) * mm, "mid": v(2.19, 18.44) * mm, "end": v(2.09, 18.4) * mm});
            skLineSegment(sketch, "E42.11.0.7", {"start": v(2.09, 18.4) * mm, "end": v(1.83, 18.4) * mm});
            skArc(sketch, "E42.12.0.0", {"start": v(5.33, 18.85) * mm, "mid": v(5.12, 19.07) * mm, "end": v(4.83, 19.16) * mm});
            skArc(sketch, "E42.12.0.1", {"start": v(5.42, 18.54) * mm, "mid": v(5.39, 18.7) * mm, "end": v(5.33, 18.85) * mm});
            skArc(sketch, "E42.12.0.2", {"start": v(5.42, 18.54) * mm, "mid": v(5.47, 18.44) * mm, "end": v(5.57, 18.4) * mm});
            skLineSegment(sketch, "E42.12.0.3", {"start": v(5.57, 18.4) * mm, "end": v(5.83, 18.4) * mm});
            skArc(sketch, "E42.12.0.4", {"start": v(4.33, 18.85) * mm, "mid": v(4.53, 19.07) * mm, "end": v(4.83, 19.16) * mm});
            skArc(sketch, "E42.12.0.5", {"start": v(4.24, 18.54) * mm, "mid": v(4.27, 18.7) * mm, "end": v(4.33, 18.85) * mm});
            skArc(sketch, "E42.12.0.6", {"start": v(4.24, 18.54) * mm, "mid": v(4.19, 18.44) * mm, "end": v(4.09, 18.4) * mm});
            skLineSegment(sketch, "E42.12.0.7", {"start": v(4.09, 18.4) * mm, "end": v(3.83, 18.4) * mm});
            skArc(sketch, "E42.13.0.0", {"start": v(7.33, 18.85) * mm, "mid": v(7.12, 19.07) * mm, "end": v(6.83, 19.16) * mm});
            skArc(sketch, "E42.13.0.1", {"start": v(7.42, 18.54) * mm, "mid": v(7.39, 18.7) * mm, "end": v(7.33, 18.85) * mm});
            skArc(sketch, "E42.13.0.2", {"start": v(7.42, 18.54) * mm, "mid": v(7.47, 18.44) * mm, "end": v(7.57, 18.4) * mm});
            skLineSegment(sketch, "E42.13.0.3", {"start": v(7.57, 18.4) * mm, "end": v(7.83, 18.4) * mm});
            skArc(sketch, "E42.13.0.4", {"start": v(6.33, 18.85) * mm, "mid": v(6.53, 19.07) * mm, "end": v(6.83, 19.16) * mm});
            skArc(sketch, "E42.13.0.5", {"start": v(6.24, 18.54) * mm, "mid": v(6.27, 18.7) * mm, "end": v(6.33, 18.85) * mm});
            skArc(sketch, "E42.13.0.6", {"start": v(6.24, 18.54) * mm, "mid": v(6.19, 18.44) * mm, "end": v(6.09, 18.4) * mm});
            skLineSegment(sketch, "E42.13.0.7", {"start": v(6.09, 18.4) * mm, "end": v(5.83, 18.4) * mm});
            skArc(sketch, "E42.14.0.0", {"start": v(9.33, 18.85) * mm, "mid": v(9.12, 19.07) * mm, "end": v(8.83, 19.16) * mm});
            skArc(sketch, "E42.14.0.1", {"start": v(9.42, 18.54) * mm, "mid": v(9.39, 18.7) * mm, "end": v(9.33, 18.85) * mm});
            skArc(sketch, "E42.14.0.2", {"start": v(9.42, 18.54) * mm, "mid": v(9.47, 18.44) * mm, "end": v(9.57, 18.4) * mm});
            skLineSegment(sketch, "E42.14.0.3", {"start": v(9.57, 18.4) * mm, "end": v(9.83, 18.4) * mm});
            skArc(sketch, "E42.14.0.4", {"start": v(8.33, 18.85) * mm, "mid": v(8.53, 19.07) * mm, "end": v(8.83, 19.16) * mm});
            skArc(sketch, "E42.14.0.5", {"start": v(8.24, 18.54) * mm, "mid": v(8.27, 18.7) * mm, "end": v(8.33, 18.85) * mm});
            skArc(sketch, "E42.14.0.6", {"start": v(8.24, 18.54) * mm, "mid": v(8.19, 18.44) * mm, "end": v(8.09, 18.4) * mm});
            skLineSegment(sketch, "E42.14.0.7", {"start": v(8.09, 18.4) * mm, "end": v(7.83, 18.4) * mm});
            skArc(sketch, "E42.15.0.0", {"start": v(11.33, 18.85) * mm, "mid": v(11.12, 19.07) * mm, "end": v(10.83, 19.16) * mm});
            skArc(sketch, "E42.15.0.1", {"start": v(11.42, 18.54) * mm, "mid": v(11.39, 18.7) * mm, "end": v(11.33, 18.85) * mm});
            skArc(sketch, "E42.15.0.2", {"start": v(11.42, 18.54) * mm, "mid": v(11.47, 18.44) * mm, "end": v(11.57, 18.4) * mm});
            skLineSegment(sketch, "E42.15.0.3", {"start": v(11.57, 18.4) * mm, "end": v(11.83, 18.4) * mm});
            skArc(sketch, "E42.15.0.4", {"start": v(10.33, 18.85) * mm, "mid": v(10.53, 19.07) * mm, "end": v(10.83, 19.16) * mm});
            skArc(sketch, "E42.15.0.5", {"start": v(10.24, 18.54) * mm, "mid": v(10.27, 18.7) * mm, "end": v(10.33, 18.85) * mm});
            skArc(sketch, "E42.15.0.6", {"start": v(10.24, 18.54) * mm, "mid": v(10.19, 18.44) * mm, "end": v(10.09, 18.4) * mm});
            skLineSegment(sketch, "E42.15.0.7", {"start": v(10.09, 18.4) * mm, "end": v(9.83, 18.4) * mm});
            skArc(sketch, "E42.16.0.0", {"start": v(13.33, 18.85) * mm, "mid": v(13.12, 19.07) * mm, "end": v(12.83, 19.16) * mm});
            skArc(sketch, "E42.16.0.1", {"start": v(13.42, 18.54) * mm, "mid": v(13.39, 18.7) * mm, "end": v(13.33, 18.85) * mm});
            skArc(sketch, "E42.16.0.2", {"start": v(13.42, 18.54) * mm, "mid": v(13.47, 18.44) * mm, "end": v(13.57, 18.4) * mm});
            skLineSegment(sketch, "E42.16.0.3", {"start": v(13.57, 18.4) * mm, "end": v(13.83, 18.4) * mm});
            skArc(sketch, "E42.16.0.4", {"start": v(12.33, 18.85) * mm, "mid": v(12.53, 19.07) * mm, "end": v(12.83, 19.16) * mm});
            skArc(sketch, "E42.16.0.5", {"start": v(12.24, 18.54) * mm, "mid": v(12.27, 18.7) * mm, "end": v(12.33, 18.85) * mm});
            skArc(sketch, "E42.16.0.6", {"start": v(12.24, 18.54) * mm, "mid": v(12.19, 18.44) * mm, "end": v(12.09, 18.4) * mm});
            skLineSegment(sketch, "E42.16.0.7", {"start": v(12.09, 18.4) * mm, "end": v(11.83, 18.4) * mm});
            skArc(sketch, "E42.17.0.0", {"start": v(15.33, 18.85) * mm, "mid": v(15.12, 19.07) * mm, "end": v(14.83, 19.16) * mm});
            skArc(sketch, "E42.17.0.1", {"start": v(15.42, 18.54) * mm, "mid": v(15.39, 18.7) * mm, "end": v(15.33, 18.85) * mm});
            skArc(sketch, "E42.17.0.2", {"start": v(15.42, 18.54) * mm, "mid": v(15.47, 18.44) * mm, "end": v(15.57, 18.4) * mm});
            skLineSegment(sketch, "E42.17.0.3", {"start": v(15.57, 18.4) * mm, "end": v(15.83, 18.4) * mm});
            skArc(sketch, "E42.17.0.4", {"start": v(14.33, 18.85) * mm, "mid": v(14.53, 19.07) * mm, "end": v(14.83, 19.16) * mm});
            skArc(sketch, "E42.17.0.5", {"start": v(14.24, 18.54) * mm, "mid": v(14.27, 18.7) * mm, "end": v(14.33, 18.85) * mm});
            skArc(sketch, "E42.17.0.6", {"start": v(14.24, 18.54) * mm, "mid": v(14.19, 18.44) * mm, "end": v(14.09, 18.4) * mm});
            skLineSegment(sketch, "E42.17.0.7", {"start": v(14.09, 18.4) * mm, "end": v(13.83, 18.4) * mm});
            skArc(sketch, "E42.18.0.0", {"start": v(17.33, 18.85) * mm, "mid": v(17.12, 19.07) * mm, "end": v(16.83, 19.16) * mm});
            skArc(sketch, "E42.18.0.1", {"start": v(17.42, 18.54) * mm, "mid": v(17.39, 18.7) * mm, "end": v(17.33, 18.85) * mm});
            skArc(sketch, "E42.18.0.2", {"start": v(17.42, 18.54) * mm, "mid": v(17.47, 18.44) * mm, "end": v(17.57, 18.4) * mm});
            skLineSegment(sketch, "E42.18.0.3", {"start": v(17.57, 18.4) * mm, "end": v(17.83, 18.4) * mm});
            skArc(sketch, "E42.18.0.4", {"start": v(16.33, 18.85) * mm, "mid": v(16.53, 19.07) * mm, "end": v(16.83, 19.16) * mm});
            skArc(sketch, "E42.18.0.5", {"start": v(16.24, 18.54) * mm, "mid": v(16.27, 18.7) * mm, "end": v(16.33, 18.85) * mm});
            skArc(sketch, "E42.18.0.6", {"start": v(16.24, 18.54) * mm, "mid": v(16.19, 18.44) * mm, "end": v(16.09, 18.4) * mm});
            skLineSegment(sketch, "E42.18.0.7", {"start": v(16.09, 18.4) * mm, "end": v(15.83, 18.4) * mm});
            skArc(sketch, "E42.19.0.0", {"start": v(19.33, 18.85) * mm, "mid": v(19.12, 19.07) * mm, "end": v(18.83, 19.16) * mm});
            skArc(sketch, "E42.19.0.1", {"start": v(19.42, 18.54) * mm, "mid": v(19.39, 18.7) * mm, "end": v(19.33, 18.85) * mm});
            skArc(sketch, "E42.19.0.2", {"start": v(19.42, 18.54) * mm, "mid": v(19.47, 18.44) * mm, "end": v(19.57, 18.4) * mm});
            skLineSegment(sketch, "E42.19.0.3", {"start": v(19.57, 18.4) * mm, "end": v(19.83, 18.4) * mm});
            skArc(sketch, "E42.19.0.4", {"start": v(18.33, 18.85) * mm, "mid": v(18.53, 19.07) * mm, "end": v(18.83, 19.16) * mm});
            skArc(sketch, "E42.19.0.5", {"start": v(18.24, 18.54) * mm, "mid": v(18.27, 18.7) * mm, "end": v(18.33, 18.85) * mm});
            skArc(sketch, "E42.19.0.6", {"start": v(18.24, 18.54) * mm, "mid": v(18.19, 18.44) * mm, "end": v(18.09, 18.4) * mm});
            skLineSegment(sketch, "E42.19.0.7", {"start": v(18.09, 18.4) * mm, "end": v(17.83, 18.4) * mm});
            skLineSegment(sketch, "E42.direction1", {"start": v(-20.17, 18.4) * mm, "end": v(-18.17, 18.4) * mm, "construction": true});
            skLineSegment(sketch, "E43", {"start": v(19.83, 18.4) * mm, "end": v(19.83, 17.78) * mm});
            skLineSegment(sketch, "E44", {"start": v(19.83, 17.78) * mm, "end": v(-18.17, 17.78) * mm});
            skLineSegment(sketch, "E45.bottom", {"start": v(-210.4, 20.6) * mm, "end": v(266.6, 20.6) * mm});
            skArc(sketch, "E46", {"start": v(266.6, 21.97) * mm, "mid": v(277.6, 32.97) * mm, "end": v(266.6, 43.97) * mm});
            skLineSegment(sketch, "E47.MirrorCS", {"start": v(-220.4, 43.97) * mm, "end": v(266.6, 43.97) * mm});
            skLineSegment(sketch, "E48.MirrorCS", {"start": v(-220.4, 45.35) * mm, "end": v(266.6, 45.35) * mm});
            skArc(sketch, "E49", {"start": v(-210.4, 20.6) * mm, "mid": v(-218.18, 17.37) * mm, "end": v(-221.4, 9.6) * mm});
            skLineSegment(sketch, "E50", {"start": v(-221.4, 9.6) * mm, "end": v(-221.4, -455.65) * mm});
            skLineSegment(sketch, "E51", {"start": v(-222.79, -455.65) * mm, "end": v(-222.79, 9.6) * mm});
            skArc(sketch, "E52.0", {"start": v(-210.4, 21.97) * mm, "mid": v(-219.16, 18.35) * mm, "end": v(-222.79, 9.6) * mm});
            skLineSegment(sketch, "E53.0", {"start": v(-210.4, 21.97) * mm, "end": v(266.6, 21.97) * mm});
            skArc(sketch, "E54", {"start": v(266.6, 20.6) * mm, "mid": v(278.97, 32.97) * mm, "end": v(266.6, 45.35) * mm});
            skArc(sketch, "E55", {"start": v(-220.4, 43.97) * mm, "mid": v(-230.94, 42.6) * mm, "end": v(-235.4, 32.97) * mm});
            skLineSegment(sketch, "E56", {"start": v(-235.4, 32.97) * mm, "end": v(-235.4, -507.03) * mm});
            skLineSegment(sketch, "E57", {"start": v(-236.79, -507.03) * mm, "end": v(-236.79, 32.97) * mm});
            skArc(sketch, "E58.trimOffspring", {"start": v(-220.4, 45.35) * mm, "mid": v(-231.91, 43.55) * mm, "end": v(-236.79, 32.97) * mm});
            skLineSegment(sketch, "E59.MirrorCS", {"start": v(-224.4, -518.03) * mm, "end": v(291.6, -518.03) * mm});
            skLineSegment(sketch, "E60.MirrorCS", {"start": v(-210.4, -494.65) * mm, "end": v(305.6, -494.65) * mm});
            skLineSegment(sketch, "E61.MirrorCS", {"start": v(-210.4, -496.03) * mm, "end": v(305.6, -496.03) * mm});
            skLineSegment(sketch, "E62.MirrorCS", {"start": v(-224.4, -519.4) * mm, "end": v(291.6, -519.4) * mm});
            skArc(sketch, "E63.MirrorCS", {"start": v(-224.4, -518.03) * mm, "mid": v(-232.18, -514.8) * mm, "end": v(-235.4, -507.03) * mm});
            skArc(sketch, "E64.MirrorCS", {"start": v(-210.4, -496.03) * mm, "mid": v(-219.16, -492.4) * mm, "end": v(-222.79, -483.65) * mm});
            skArc(sketch, "E65.MirrorCS", {"start": v(-224.4, -519.4) * mm, "mid": v(-233.16, -515.78) * mm, "end": v(-236.79, -507.03) * mm});
            skArc(sketch, "E66.MirrorCS", {"start": v(-210.4, -494.65) * mm, "mid": v(-218.18, -491.42) * mm, "end": v(-221.4, -483.65) * mm});
            skLineSegment(sketch, "E67", {"start": v(-222.79, -483.65) * mm, "end": v(-221.4, -483.65) * mm});
            skLineSegment(sketch, "E68", {"start": v(-222.79, -455.65) * mm, "end": v(-221.4, -455.65) * mm});
            skLineSegment(sketch, "E69", {"start": v(291.6, -518.03) * mm, "end": v(301.6, -518.03) * mm});
            skLineSegment(sketch, "E70", {"start": v(301.6, -519.4) * mm, "end": v(291.6, -519.4) * mm});
            skArc(sketch, "E71", {"start": v(301.6, -518.03) * mm, "mid": v(305.84, -507.78) * mm, "end": v(295.6, -512.03) * mm});
            skArc(sketch, "E72.0", {"start": v(301.6, -519.4) * mm, "mid": v(306.81, -506.8) * mm, "end": v(294.21, -512.03) * mm});
            skLineSegment(sketch, "E73", {"start": v(305.6, -494.65) * mm, "end": v(305.6, -496.03) * mm});
            skLineSegment(sketch, "E74", {"start": v(295.6, -512.03) * mm, "end": v(294.21, -512.03) * mm});
            skSolve(sketch);
        }
        {
            var Q0;
            Q0=makeQuery(id+"F0.imprint","IMPRINT",FACE,{"disambiguationData":[TD([[makeQuery(id+"F0.imprint","IMPRINT",EDGE,{"derivedFrom":sQuery(id+"F0.wireOp",EDGE,"E15")}),-1.0]])]});
            extrude(context, id + "F1", {"entities" : qUnion([Q0]), "depth" : 7.5 * mm});
        }
        {
            var Q0;
            Q0=makeQuery(id+"F1.opExtrude","CAP_FACE",FACE,{"disambiguationData":[OSD([sQuery(id+"F0.wireOp",EDGE,"E15"),sQuery(id+"F0.wireOp",EDGE,"E16"),sQuery(id+"F0.wireOp",EDGE,"E17"),sQuery(id+"F0.wireOp",EDGE,"E18"),sQuery(id+"F0.wireOp",EDGE,"E19"),sQuery(id+"F0.wireOp",EDGE,"E20"),sQuery(id+"F0.wireOp",EDGE,"E21.1.0"),sQuery(id+"F0.wireOp",EDGE,"E21.1.2"),sQuery(id+"F0.wireOp",EDGE,"E21.1.3"),sQuery(id+"F0.wireOp",EDGE,"E21.1.4"),sQuery(id+"F0.wireOp",EDGE,"E21.1.5"),sQuery(id+"F0.wireOp",EDGE,"E22.3.2.0"),sQuery(id+"F0.wireOp",EDGE,"E22.5.2.0"),sQuery(id+"F0.wireOp",EDGE,"E22.9.2.0"),sQuery(id+"F0.wireOp",EDGE,"E22.13.2.0"),sQuery(id+"F0.wireOp",EDGE,"E22.17.2.0"),sQuery(id+"F0.wireOp",EDGE,"E22.3.3.0"),sQuery(id+"F0.wireOp",EDGE,"E22.5.3.0"),sQuery(id+"F0.wireOp",EDGE,"E22.9.3.0"),sQuery(id+"F0.wireOp",EDGE,"E22.13.3.0"),sQuery(id+"F0.wireOp",EDGE,"E22.17.3.0"),sQuery(id+"F0.wireOp",EDGE,"E22.3.4.0"),sQuery(id+"F0.wireOp",EDGE,"E22.5.4.0"),sQuery(id+"F0.wireOp",EDGE,"E22.9.4.0"),sQuery(id+"F0.wireOp",EDGE,"E22.13.4.0"),sQuery(id+"F0.wireOp",EDGE,"E22.17.4.0"),sQuery(id+"F0.wireOp",EDGE,"E22.3.5.0"),sQuery(id+"F0.wireOp",EDGE,"E22.5.5.0"),sQuery(id+"F0.wireOp",EDGE,"E22.9.5.0"),sQuery(id+"F0.wireOp",EDGE,"E22.13.5.0"),sQuery(id+"F0.wireOp",EDGE,"E22.17.5.0"),sQuery(id+"F0.wireOp",EDGE,"E22.3.6.0"),sQuery(id+"F0.wireOp",EDGE,"E22.5.6.0"),sQuery(id+"F0.wireOp",EDGE,"E22.9.6.0"),sQuery(id+"F0.wireOp",EDGE,"E22.13.6.0"),sQuery(id+"F0.wireOp",EDGE,"E22.17.6.0"),sQuery(id+"F0.wireOp",EDGE,"E22.3.7.0"),sQuery(id+"F0.wireOp",EDGE,"E22.5.7.0"),sQuery(id+"F0.wireOp",EDGE,"E22.9.7.0"),sQuery(id+"F0.wireOp",EDGE,"E22.13.7.0"),sQuery(id+"F0.wireOp",EDGE,"E22.17.7.0"),sQuery(id+"F0.wireOp",EDGE,"E22.3.8.0"),sQuery(id+"F0.wireOp",EDGE,"E22.5.8.0"),sQuery(id+"F0.wireOp",EDGE,"E22.9.8.0"),sQuery(id+"F0.wireOp",EDGE,"E22.13.8.0"),sQuery(id+"F0.wireOp",EDGE,"E22.17.8.0"),sQuery(id+"F0.wireOp",EDGE,"E22.3.9.0"),sQuery(id+"F0.wireOp",EDGE,"E22.5.9.0"),sQuery(id+"F0.wireOp",EDGE,"E22.9.9.0"),sQuery(id+"F0.wireOp",EDGE,"E22.13.9.0"),sQuery(id+"F0.wireOp",EDGE,"E22.17.9.0"),sQuery(id+"F0.wireOp",EDGE,"E22.3.10.0"),sQuery(id+"F0.wireOp",EDGE,"E22.5.10.0"),sQuery(id+"F0.wireOp",EDGE,"E22.9.10.0"),sQuery(id+"F0.wireOp",EDGE,"E22.13.10.0"),sQuery(id+"F0.wireOp",EDGE,"E22.17.10.0"),sQuery(id+"F0.wireOp",EDGE,"E22.3.11.0"),sQuery(id+"F0.wireOp",EDGE,"E22.5.11.0"),sQuery(id+"F0.wireOp",EDGE,"E22.9.11.0"),sQuery(id+"F0.wireOp",EDGE,"E22.13.11.0"),sQuery(id+"F0.wireOp",EDGE,"E22.17.11.0"),sQuery(id+"F0.wireOp",EDGE,"E22.3.12.0"),sQuery(id+"F0.wireOp",EDGE,"E22.5.12.0"),sQuery(id+"F0.wireOp",EDGE,"E22.9.12.0"),sQuery(id+"F0.wireOp",EDGE,"E22.13.12.0"),sQuery(id+"F0.wireOp",EDGE,"E22.17.12.0"),sQuery(id+"F0.wireOp",EDGE,"E22.3.13.0"),sQuery(id+"F0.wireOp",EDGE,"E22.5.13.0"),sQuery(id+"F0.wireOp",EDGE,"E22.9.13.0"),sQuery(id+"F0.wireOp",EDGE,"E22.13.13.0"),sQuery(id+"F0.wireOp",EDGE,"E22.17.13.0"),sQuery(id+"F0.wireOp",EDGE,"E22.3.14.0"),sQuery(id+"F0.wireOp",EDGE,"E22.5.14.0"),sQuery(id+"F0.wireOp",EDGE,"E22.9.14.0"),sQuery(id+"F0.wireOp",EDGE,"E22.13.14.0"),sQuery(id+"F0.wireOp",EDGE,"E22.17.14.0"),sQuery(id+"F0.wireOp",EDGE,"E22.3.15.0"),sQuery(id+"F0.wireOp",EDGE,"E22.5.15.0"),sQuery(id+"F0.wireOp",EDGE,"E22.9.15.0"),sQuery(id+"F0.wireOp",EDGE,"E22.13.15.0"),sQuery(id+"F0.wireOp",EDGE,"E22.17.15.0"),sQuery(id+"F0.wireOp",EDGE,"E22.3.16.0"),sQuery(id+"F0.wireOp",EDGE,"E22.5.16.0"),sQuery(id+"F0.wireOp",EDGE,"E22.9.16.0"),sQuery(id+"F0.wireOp",EDGE,"E22.13.16.0"),sQuery(id+"F0.wireOp",EDGE,"E22.17.16.0"),sQuery(id+"F0.wireOp",EDGE,"E22.3.17.0"),sQuery(id+"F0.wireOp",EDGE,"E22.5.17.0"),sQuery(id+"F0.wireOp",EDGE,"E22.9.17.0"),sQuery(id+"F0.wireOp",EDGE,"E22.13.17.0"),sQuery(id+"F0.wireOp",EDGE,"E22.17.17.0"),sQuery(id+"F0.wireOp",EDGE,"E22.3.18.0"),sQuery(id+"F0.wireOp",EDGE,"E22.5.18.0"),sQuery(id+"F0.wireOp",EDGE,"E22.9.18.0"),sQuery(id+"F0.wireOp",EDGE,"E22.13.18.0"),sQuery(id+"F0.wireOp",EDGE,"E22.17.18.0"),sQuery(id+"F0.wireOp",EDGE,"E22.3.19.0"),sQuery(id+"F0.wireOp",EDGE,"E22.5.19.0"),sQuery(id+"F0.wireOp",EDGE,"E22.9.19.0"),sQuery(id+"F0.wireOp",EDGE,"E22.13.19.0"),sQuery(id+"F0.wireOp",EDGE,"E22.17.19.0"),sQuery(id+"F0.wireOp",EDGE,"E23.trimOffspring"),sQuery(id+"F0.wireOp",EDGE,"E24.trimOffspring"),sQuery(id+"F0.wireOp",EDGE,"E25.trimOffspring"),sQuery(id+"F0.wireOp",EDGE,"E26.trimOffspring"),sQuery(id+"F0.wireOp",EDGE,"E27.trimOffspring"),sQuery(id+"F0.wireOp",EDGE,"E28.trimOffspring"),sQuery(id+"F0.wireOp",EDGE,"E29.trimOffspring"),sQuery(id+"F0.wireOp",EDGE,"E30.trimOffspring"),sQuery(id+"F0.wireOp",EDGE,"E31.trimOffspring"),sQuery(id+"F0.wireOp",EDGE,"E32.trimOffspring"),sQuery(id+"F0.wireOp",EDGE,"E33.trimOffspring"),sQuery(id+"F0.wireOp",EDGE,"E34.trimOffspring"),sQuery(id+"F0.wireOp",EDGE,"E35.trimOffspring"),sQuery(id+"F0.wireOp",EDGE,"E36.trimOffspring"),sQuery(id+"F0.wireOp",EDGE,"E37.trimOffspring"),sQuery(id+"F0.wireOp",EDGE,"E38.trimOffspring"),sQuery(id+"F0.wireOp",EDGE,"E39.trimOffspring"),sQuery(id+"F0.wireOp",EDGE,"E40.trimOffspring"),sQuery(id+"F0.wireOp",EDGE,"E41.trimOffspring")])],"isStart":false});
            var sketch = newSketch(context, id + "F2", { "sketchPlane" : qUnion([Q0])});
            skCircle(sketch, "E75", {"center": v(0, 0) * mm, "radius": 8 * mm});
            skSolve(sketch);
        }
        {
            var Q0;
            Q0=qSketchRegion(id+"F2",true);
            extrude(context, id + "F3", {"entities" : qUnion([Q0]), "operationType" : NewBodyOperationType.ADD, "depth" : 9 * mm});
        }
        {
            var Q0;
            Q0=makeQuery(id+"F1.opExtrude","CAP_FACE",FACE,{"disambiguationData":[OSD([sQuery(id+"F0.wireOp",EDGE,"E15"),sQuery(id+"F0.wireOp",EDGE,"E16"),sQuery(id+"F0.wireOp",EDGE,"E17"),sQuery(id+"F0.wireOp",EDGE,"E18"),sQuery(id+"F0.wireOp",EDGE,"E19"),sQuery(id+"F0.wireOp",EDGE,"E20"),sQuery(id+"F0.wireOp",EDGE,"E21.1.0"),sQuery(id+"F0.wireOp",EDGE,"E21.1.2"),sQuery(id+"F0.wireOp",EDGE,"E21.1.3"),sQuery(id+"F0.wireOp",EDGE,"E21.1.4"),sQuery(id+"F0.wireOp",EDGE,"E21.1.5"),sQuery(id+"F0.wireOp",EDGE,"E22.3.2.0"),sQuery(id+"F0.wireOp",EDGE,"E22.5.2.0"),sQuery(id+"F0.wireOp",EDGE,"E22.9.2.0"),sQuery(id+"F0.wireOp",EDGE,"E22.13.2.0"),sQuery(id+"F0.wireOp",EDGE,"E22.17.2.0"),sQuery(id+"F0.wireOp",EDGE,"E22.3.3.0"),sQuery(id+"F0.wireOp",EDGE,"E22.5.3.0"),sQuery(id+"F0.wireOp",EDGE,"E22.9.3.0"),sQuery(id+"F0.wireOp",EDGE,"E22.13.3.0"),sQuery(id+"F0.wireOp",EDGE,"E22.17.3.0"),sQuery(id+"F0.wireOp",EDGE,"E22.3.4.0"),sQuery(id+"F0.wireOp",EDGE,"E22.5.4.0"),sQuery(id+"F0.wireOp",EDGE,"E22.9.4.0"),sQuery(id+"F0.wireOp",EDGE,"E22.13.4.0"),sQuery(id+"F0.wireOp",EDGE,"E22.17.4.0"),sQuery(id+"F0.wireOp",EDGE,"E22.3.5.0"),sQuery(id+"F0.wireOp",EDGE,"E22.5.5.0"),sQuery(id+"F0.wireOp",EDGE,"E22.9.5.0"),sQuery(id+"F0.wireOp",EDGE,"E22.13.5.0"),sQuery(id+"F0.wireOp",EDGE,"E22.17.5.0"),sQuery(id+"F0.wireOp",EDGE,"E22.3.6.0"),sQuery(id+"F0.wireOp",EDGE,"E22.5.6.0"),sQuery(id+"F0.wireOp",EDGE,"E22.9.6.0"),sQuery(id+"F0.wireOp",EDGE,"E22.13.6.0"),sQuery(id+"F0.wireOp",EDGE,"E22.17.6.0"),sQuery(id+"F0.wireOp",EDGE,"E22.3.7.0"),sQuery(id+"F0.wireOp",EDGE,"E22.5.7.0"),sQuery(id+"F0.wireOp",EDGE,"E22.9.7.0"),sQuery(id+"F0.wireOp",EDGE,"E22.13.7.0"),sQuery(id+"F0.wireOp",EDGE,"E22.17.7.0"),sQuery(id+"F0.wireOp",EDGE,"E22.3.8.0"),sQuery(id+"F0.wireOp",EDGE,"E22.5.8.0"),sQuery(id+"F0.wireOp",EDGE,"E22.9.8.0"),sQuery(id+"F0.wireOp",EDGE,"E22.13.8.0"),sQuery(id+"F0.wireOp",EDGE,"E22.17.8.0"),sQuery(id+"F0.wireOp",EDGE,"E22.3.9.0"),sQuery(id+"F0.wireOp",EDGE,"E22.5.9.0"),sQuery(id+"F0.wireOp",EDGE,"E22.9.9.0"),sQuery(id+"F0.wireOp",EDGE,"E22.13.9.0"),sQuery(id+"F0.wireOp",EDGE,"E22.17.9.0"),sQuery(id+"F0.wireOp",EDGE,"E22.3.10.0"),sQuery(id+"F0.wireOp",EDGE,"E22.5.10.0"),sQuery(id+"F0.wireOp",EDGE,"E22.9.10.0"),sQuery(id+"F0.wireOp",EDGE,"E22.13.10.0"),sQuery(id+"F0.wireOp",EDGE,"E22.17.10.0"),sQuery(id+"F0.wireOp",EDGE,"E22.3.11.0"),sQuery(id+"F0.wireOp",EDGE,"E22.5.11.0"),sQuery(id+"F0.wireOp",EDGE,"E22.9.11.0"),sQuery(id+"F0.wireOp",EDGE,"E22.13.11.0"),sQuery(id+"F0.wireOp",EDGE,"E22.17.11.0"),sQuery(id+"F0.wireOp",EDGE,"E22.3.12.0"),sQuery(id+"F0.wireOp",EDGE,"E22.5.12.0"),sQuery(id+"F0.wireOp",EDGE,"E22.9.12.0"),sQuery(id+"F0.wireOp",EDGE,"E22.13.12.0"),sQuery(id+"F0.wireOp",EDGE,"E22.17.12.0"),sQuery(id+"F0.wireOp",EDGE,"E22.3.13.0"),sQuery(id+"F0.wireOp",EDGE,"E22.5.13.0"),sQuery(id+"F0.wireOp",EDGE,"E22.9.13.0"),sQuery(id+"F0.wireOp",EDGE,"E22.13.13.0"),sQuery(id+"F0.wireOp",EDGE,"E22.17.13.0"),sQuery(id+"F0.wireOp",EDGE,"E22.3.14.0"),sQuery(id+"F0.wireOp",EDGE,"E22.5.14.0"),sQuery(id+"F0.wireOp",EDGE,"E22.9.14.0"),sQuery(id+"F0.wireOp",EDGE,"E22.13.14.0"),sQuery(id+"F0.wireOp",EDGE,"E22.17.14.0"),sQuery(id+"F0.wireOp",EDGE,"E22.3.15.0"),sQuery(id+"F0.wireOp",EDGE,"E22.5.15.0"),sQuery(id+"F0.wireOp",EDGE,"E22.9.15.0"),sQuery(id+"F0.wireOp",EDGE,"E22.13.15.0"),sQuery(id+"F0.wireOp",EDGE,"E22.17.15.0"),sQuery(id+"F0.wireOp",EDGE,"E22.3.16.0"),sQuery(id+"F0.wireOp",EDGE,"E22.5.16.0"),sQuery(id+"F0.wireOp",EDGE,"E22.9.16.0"),sQuery(id+"F0.wireOp",EDGE,"E22.13.16.0"),sQuery(id+"F0.wireOp",EDGE,"E22.17.16.0"),sQuery(id+"F0.wireOp",EDGE,"E22.3.17.0"),sQuery(id+"F0.wireOp",EDGE,"E22.5.17.0"),sQuery(id+"F0.wireOp",EDGE,"E22.9.17.0"),sQuery(id+"F0.wireOp",EDGE,"E22.13.17.0"),sQuery(id+"F0.wireOp",EDGE,"E22.17.17.0"),sQuery(id+"F0.wireOp",EDGE,"E22.3.18.0"),sQuery(id+"F0.wireOp",EDGE,"E22.5.18.0"),sQuery(id+"F0.wireOp",EDGE,"E22.9.18.0"),sQuery(id+"F0.wireOp",EDGE,"E22.13.18.0"),sQuery(id+"F0.wireOp",EDGE,"E22.17.18.0"),sQuery(id+"F0.wireOp",EDGE,"E22.3.19.0"),sQuery(id+"F0.wireOp",EDGE,"E22.5.19.0"),sQuery(id+"F0.wireOp",EDGE,"E22.9.19.0"),sQuery(id+"F0.wireOp",EDGE,"E22.13.19.0"),sQuery(id+"F0.wireOp",EDGE,"E22.17.19.0"),sQuery(id+"F0.wireOp",EDGE,"E23.trimOffspring"),sQuery(id+"F0.wireOp",EDGE,"E24.trimOffspring"),sQuery(id+"F0.wireOp",EDGE,"E25.trimOffspring"),sQuery(id+"F0.wireOp",EDGE,"E26.trimOffspring"),sQuery(id+"F0.wireOp",EDGE,"E27.trimOffspring"),sQuery(id+"F0.wireOp",EDGE,"E28.trimOffspring"),sQuery(id+"F0.wireOp",EDGE,"E29.trimOffspring"),sQuery(id+"F0.wireOp",EDGE,"E30.trimOffspring"),sQuery(id+"F0.wireOp",EDGE,"E31.trimOffspring"),sQuery(id+"F0.wireOp",EDGE,"E32.trimOffspring"),sQuery(id+"F0.wireOp",EDGE,"E33.trimOffspring"),sQuery(id+"F0.wireOp",EDGE,"E34.trimOffspring"),sQuery(id+"F0.wireOp",EDGE,"E35.trimOffspring"),sQuery(id+"F0.wireOp",EDGE,"E36.trimOffspring"),sQuery(id+"F0.wireOp",EDGE,"E37.trimOffspring"),sQuery(id+"F0.wireOp",EDGE,"E38.trimOffspring"),sQuery(id+"F0.wireOp",EDGE,"E39.trimOffspring"),sQuery(id+"F0.wireOp",EDGE,"E40.trimOffspring"),sQuery(id+"F0.wireOp",EDGE,"E41.trimOffspring")])],"isStart":true});
            var sketch = newSketch(context, id + "F4", { "sketchPlane" : qUnion([Q0])});
            skCircle(sketch, "E76", {"center": v(0, 0) * mm, "radius": 8 * mm});
            skSolve(sketch);
        }
        {
            var Q0;
            Q0=qSketchRegion(id+"F4",true);
            extrude(context, id + "F5", {"entities" : qUnion([Q0]), "operationType" : NewBodyOperationType.ADD, "depth" : 1.5 * mm});
        }
        {
            var Q0;
            Q0=makeQuery(id+"F5.opExtrude","CAP_FACE",FACE,{"disambiguationData":[OSD([sQuery(id+"F4.wireOp",EDGE,"E76")])],"isStart":false});
            var sketch = newSketch(context, id + "F6", { "sketchPlane" : qUnion([Q0])});
            skCircle(sketch, "E77", {"center": v(0, 0) * mm, "radius": 2.5 * mm});
            skSolve(sketch);
        }
        {
            var Q0;
            Q0=qSketchRegion(id+"F6",true);
            extrude(context, id + "F7", {"entities" : qUnion([Q0]), "operationType" : NewBodyOperationType.REMOVE, "endBound" : BoundingType.THROUGH_ALL, "oppositeDirection" : true, "depth" : 25 * mm});
        }
        {
            var Q0;
            Q0=qCreatedBy(makeId("Right.planeOp"),FACE);
            var sketch = newSketch(context, id + "F8", { "sketchPlane" : qUnion([Q0])});
            skCircle(sketch, "E78", {"center": v(0, 12) * mm, "radius": 1.5 * mm});
            skSolve(sketch);
        }
        {
            var Q0;
            Q0=qSketchRegion(id+"F8",true);
            extrude(context, id + "F9", {"entities" : qUnion([Q0]), "operationType" : NewBodyOperationType.REMOVE, "endBound" : BoundingType.THROUGH_ALL, "oppositeDirection" : true, "depth" : 25 * mm});
        }
        {
            var Q0;
            Q0=qCreatedBy(makeId("Front.planeOp"),FACE);
            var sketch = newSketch(context, id + "F10", { "sketchPlane" : qUnion([Q0])});
            skCircle(sketch, "E79", {"center": v(0, 12) * mm, "radius": 1.5 * mm});
            skSolve(sketch);
        }
        {
            var Q0;
            Q0=qSketchRegion(id+"F10",true);
            extrude(context, id + "F11", {"entities" : qUnion([Q0]), "operationType" : NewBodyOperationType.REMOVE, "endBound" : BoundingType.THROUGH_ALL, "oppositeDirection" : true, "depth" : 25 * mm});
        }
        {
            var Q0;
            Q0=makeQuery(id+"F0.imprint","IMPRINT",FACE,{"disambiguationData":[TD([[makeQuery(id+"F0.imprint","IMPRINT",EDGE,{"derivedFrom":sQuery(id+"F0.wireOp",EDGE,"E1")}),-1.0]])]});
            var Q1;
            Q1=makeQuery(id+"F0.imprint","IMPRINT",FACE,{"disambiguationData":[TD([[makeQuery(id+"F0.imprint","IMPRINT",EDGE,{"derivedFrom":sQuery(id+"F0.wireOp",EDGE,"E45.bottom")}),1.0]])]});
            extrude(context, id + "F12", {"entities" : qUnion([Q0, Q1]), "depth" : 6 * mm});
        }
    });
